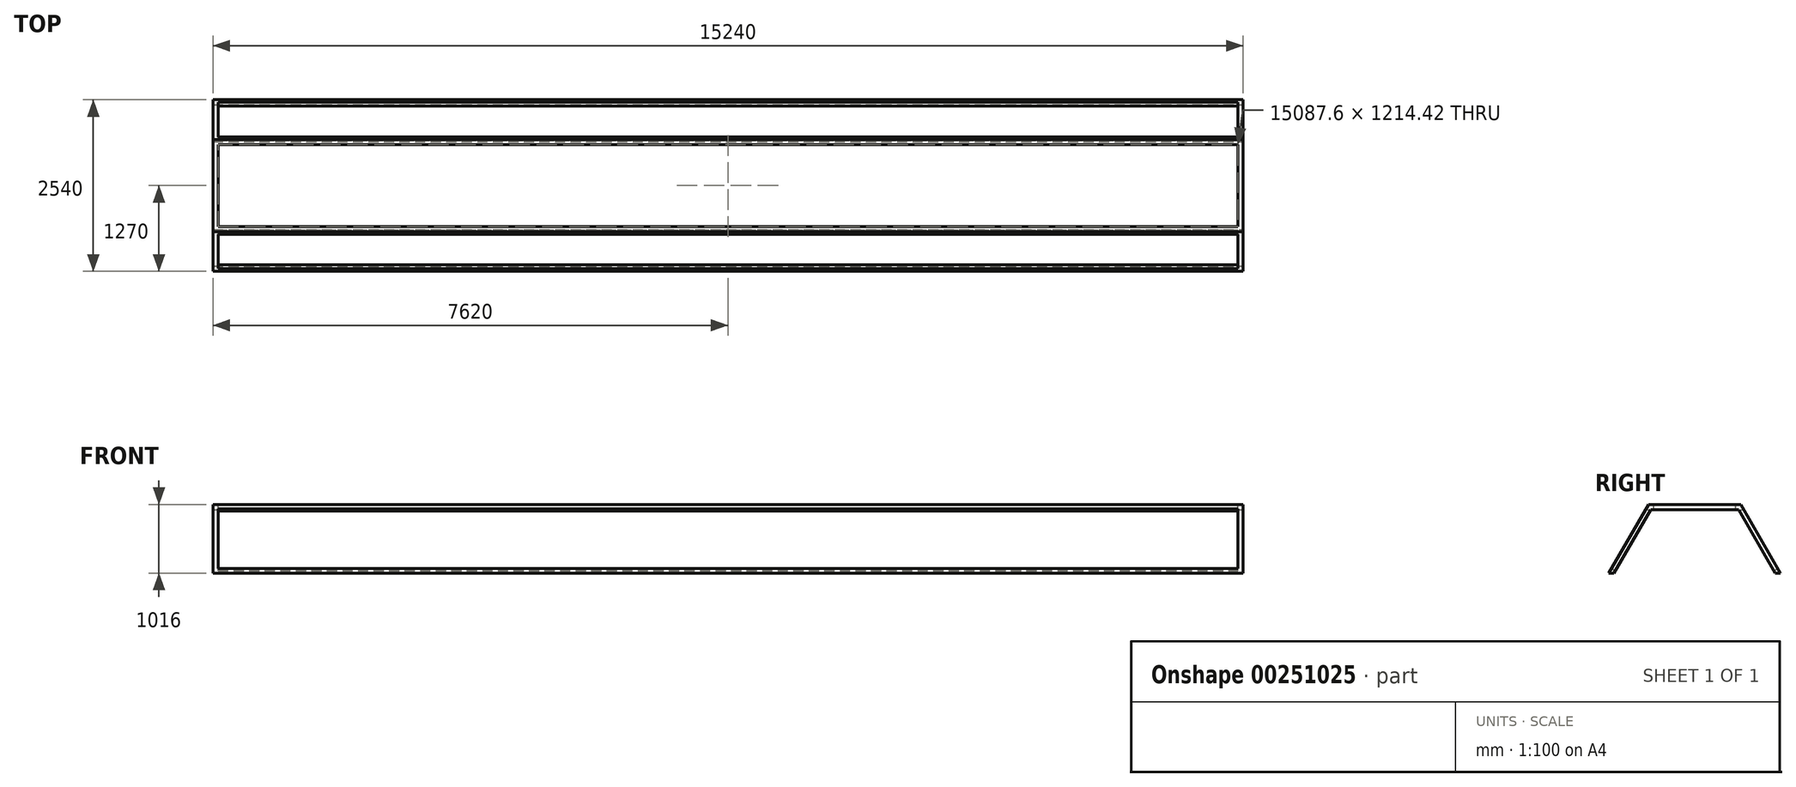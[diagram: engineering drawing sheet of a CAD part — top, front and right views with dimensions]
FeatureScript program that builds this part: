
annotation { "Feature Type Name" : "Feature", "Feature Type Description" : "" }
export const myFeature = defineFeature(function(context is Context, id is Id, definition is map)
    precondition{}
    {
        {
            var Q0;
            Q0=qCreatedBy(makeId("Right.planeOp"),FACE);
            var sketch = newSketch(context, id + "F0", { "sketchPlane" : qUnion([Q0])});
            skLineSegment(sketch, "E0", {"start": v(-627.03, 0) * mm, "end": v(-550.83, 0) * mm});
            skLineSegment(sketch, "E1", {"start": v(-627.03, 0) * mm, "end": v(-40.44, 1016) * mm});
            skLineSegment(sketch, "E2", {"start": v(-40.44, 1016) * mm, "end": v(1326.38, 1016) * mm});
            skLineSegment(sketch, "E3", {"start": v(-550.83, 0) * mm, "end": v(-8.23, 939.8) * mm});
            skLineSegment(sketch, "E4.MirrorCS", {"start": v(1836.77, 0) * mm, "end": v(1294.18, 939.8) * mm});
            skLineSegment(sketch, "E5.MirrorCS", {"start": v(1912.97, 0) * mm, "end": v(1326.38, 1016) * mm});
            skLineSegment(sketch, "E6", {"start": v(1912.97, 0) * mm, "end": v(1836.77, 0) * mm});
            skLineSegment(sketch, "E7.0", {"start": v(-8.23, 939.8) * mm, "end": v(1294.18, 939.8) * mm});
            skPoint(sketch, "E8.orphan", {"position": v(1250.18, 1016) * mm});
            skPoint(sketch, "E9.orphan", {"position": v(35.76, 1016) * mm});
            skPoint(sketch, "E10.orphan", {"position": v(642.97, 1016) * mm});
            skSolve(sketch);
        }
        {
            var Q0;
            Q0=qSketchRegion(id+"F0",true);
            extrude(context, id + "F1", {"entities" : qUnion([Q0]), "oppositeDirection" : true, "depth" : 15240 * mm});
        }
        {
            var Q0;
            Q0=makeQuery(id+"F1.opExtrude","SWEPT_FACE",FACE,{"disambiguationData":[OSD([sQuery(id+"F0.wireOp",EDGE,"E1")])]});
            var sketch = newSketch(context, id + "F2", { "sketchPlane" : qUnion([Q0])});
            skLineSegment(sketch, "E11", {"start": v(-15240, 859.66) * mm, "end": v(0, 859.66) * mm});
            skLineSegment(sketch, "E12.0", {"start": v(-15163.8, 783.46) * mm, "end": v(-76.2, 783.46) * mm});
            skLineSegment(sketch, "E13", {"start": v(-15240, 859.66) * mm, "end": v(-15240, -313.51) * mm});
            skLineSegment(sketch, "E14.0", {"start": v(-15163.8, 783.46) * mm, "end": v(-15163.8, -237.31) * mm});
            skLineSegment(sketch, "E15", {"start": v(-15240, -313.51) * mm, "end": v(0, -313.51) * mm});
            skLineSegment(sketch, "E16.0", {"start": v(-15163.8, -237.31) * mm, "end": v(-76.2, -237.31) * mm});
            skLineSegment(sketch, "E17", {"start": v(0, 859.66) * mm, "end": v(0, -313.51) * mm});
            skLineSegment(sketch, "E18.0", {"start": v(-76.2, 783.46) * mm, "end": v(-76.2, -237.31) * mm});
            skSolve(sketch);
        }
        {
            var Q0;
            Q0=makeQuery(id+"F2.imprint","IMPRINT",FACE,{"disambiguationData":[TD([[makeQuery(id+"F2.imprint","IMPRINT",EDGE,{"derivedFrom":sQuery(id+"F2.wireOp",EDGE,"E12.0")}),-1.0]])]});
            extrude(context, id + "F3", {"entities" : qUnion([Q0]), "operationType" : NewBodyOperationType.REMOVE, "oppositeDirection" : true, "depth" : 76.2 * mm});
        }
        {
            var Q0;
            Q0=makeQuery(id+"F1.opExtrude","SWEPT_FACE",FACE,{"disambiguationData":[OSD([sQuery(id+"F0.wireOp",EDGE,"E2")])]});
            var sketch = newSketch(context, id + "F4", { "sketchPlane" : qUnion([Q0])});
            skLineSegment(sketch, "E19", {"start": v(-15240, 1326.38) * mm, "end": v(0, 1326.38) * mm});
            skLineSegment(sketch, "E20", {"start": v(0, 1326.38) * mm, "end": v(0, -40.44) * mm});
            skLineSegment(sketch, "E21", {"start": v(0, -40.44) * mm, "end": v(-15240, -40.44) * mm});
            skLineSegment(sketch, "E22", {"start": v(-15240, -40.44) * mm, "end": v(-15240, 1326.38) * mm});
            skLineSegment(sketch, "E23.0", {"start": v(-15163.8, 1250.18) * mm, "end": v(-76.2, 1250.18) * mm});
            skLineSegment(sketch, "E24.0", {"start": v(-15163.8, 35.76) * mm, "end": v(-15163.8, 1250.18) * mm});
            skLineSegment(sketch, "E25.0", {"start": v(-76.2, 35.76) * mm, "end": v(-15163.8, 35.76) * mm});
            skLineSegment(sketch, "E26.0", {"start": v(-76.2, 1250.18) * mm, "end": v(-76.2, 35.76) * mm});
            skSolve(sketch);
        }
        {
            var Q0;
            Q0=makeQuery(id+"F4.imprint","IMPRINT",FACE,{"disambiguationData":[TD([[makeQuery(id+"F4.imprint","IMPRINT",EDGE,{"derivedFrom":sQuery(id+"F4.wireOp",EDGE,"E23.0")}),-1.0]])]});
            extrude(context, id + "F5", {"entities" : qUnion([Q0]), "operationType" : NewBodyOperationType.REMOVE, "oppositeDirection" : true, "depth" : 76.2 * mm});
        }
        {
            var Q0;
            Q0=makeQuery(id+"F1.opExtrude","SWEPT_FACE",FACE,{"disambiguationData":[OSD([sQuery(id+"F0.wireOp",EDGE,"E5.MirrorCS")])]});
            var sketch = newSketch(context, id + "F6", { "sketchPlane" : qUnion([Q0])});
            skLineSegment(sketch, "E27", {"start": v(0, 216.69) * mm, "end": v(15240, 216.69) * mm});
            skLineSegment(sketch, "E28", {"start": v(15240, 216.69) * mm, "end": v(15240, -956.49) * mm});
            skLineSegment(sketch, "E29", {"start": v(15240, -956.49) * mm, "end": v(0, -956.49) * mm});
            skLineSegment(sketch, "E30", {"start": v(0, -956.49) * mm, "end": v(0, 216.69) * mm});
            skLineSegment(sketch, "E31.0", {"start": v(76.2, 140.49) * mm, "end": v(15163.8, 140.49) * mm});
            skLineSegment(sketch, "E32.0", {"start": v(76.2, -880.29) * mm, "end": v(76.2, 140.49) * mm});
            skLineSegment(sketch, "E33.0", {"start": v(15163.8, -880.29) * mm, "end": v(76.2, -880.29) * mm});
            skLineSegment(sketch, "E34.0", {"start": v(15163.8, 140.49) * mm, "end": v(15163.8, -880.29) * mm});
            skSolve(sketch);
        }
        {
            var Q0;
            Q0=makeQuery(id+"F6.imprint","IMPRINT",FACE,{"disambiguationData":[TD([[makeQuery(id+"F6.imprint","IMPRINT",EDGE,{"derivedFrom":sQuery(id+"F6.wireOp",EDGE,"E31.0")}),-1.0]])]});
            extrude(context, id + "F7", {"entities" : qUnion([Q0]), "operationType" : NewBodyOperationType.REMOVE, "oppositeDirection" : true, "depth" : 76.2 * mm});
        }
    });
